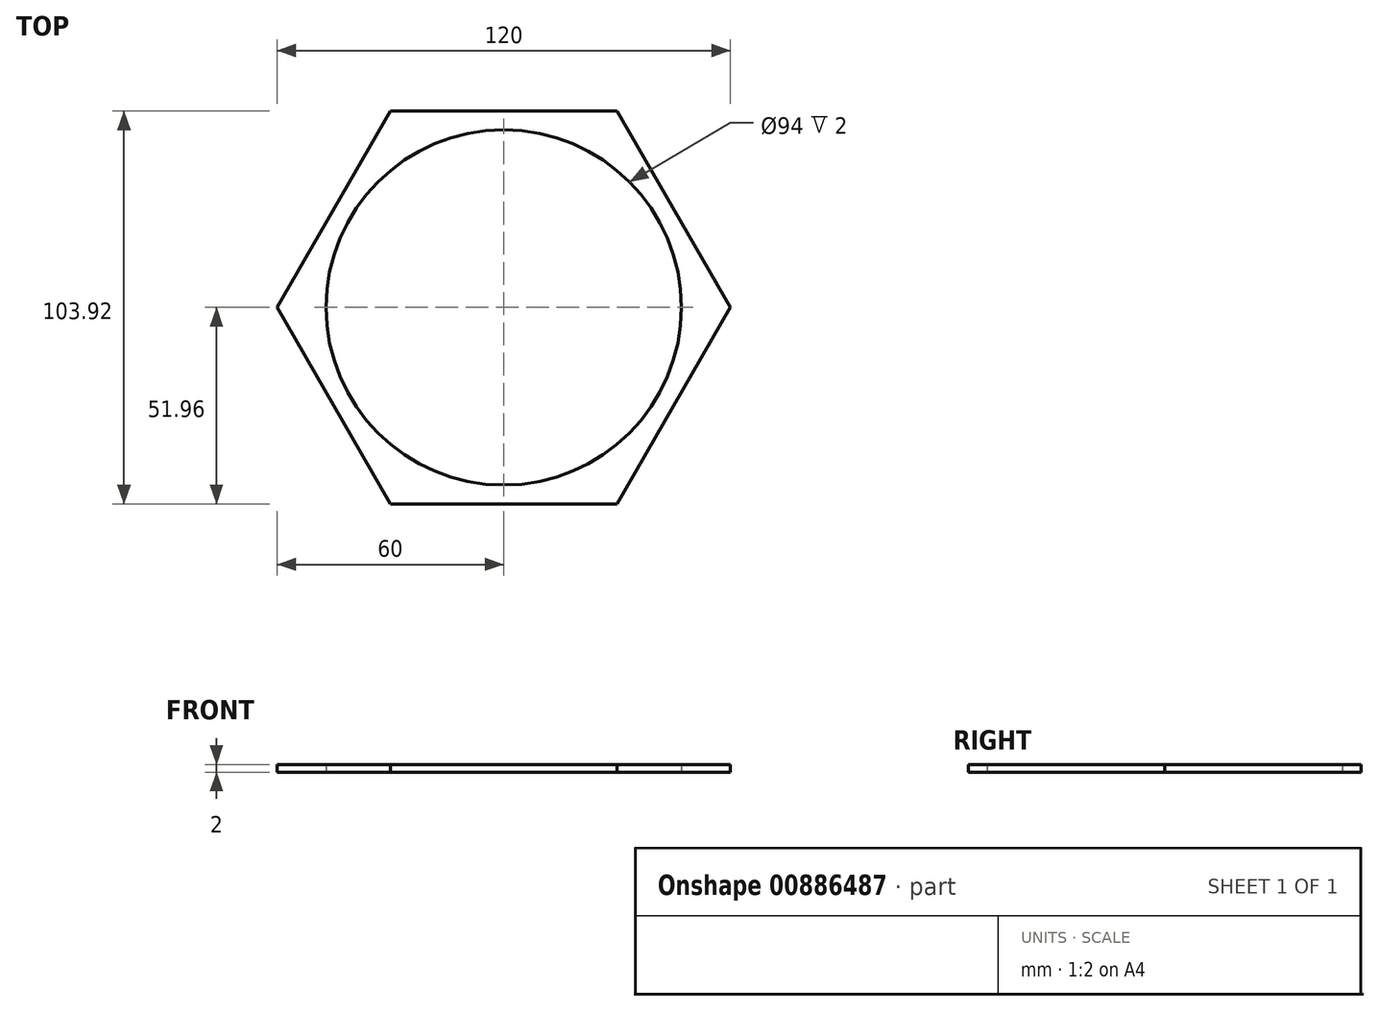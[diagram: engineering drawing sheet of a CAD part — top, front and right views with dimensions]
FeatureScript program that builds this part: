
annotation { "Feature Type Name" : "Feature", "Feature Type Description" : "" }
export const myFeature = defineFeature(function(context is Context, id is Id, definition is map)
    precondition{}
    {
        {
            var Q0;
            Q0=qCreatedBy(makeId("Top.planeOp"),FACE);
            var sketch = newSketch(context, id + "F0", { "sketchPlane" : qUnion([Q0])});
            skCircle(sketch, "E0.cCircle", {"center": v(0, 0) * mm, "radius": 60 * mm, "construction": true});
            skLineSegment(sketch, "E0.0", {"start": v(-60, 0) * mm, "end": v(-30, 51.96) * mm});
            skLineSegment(sketch, "E0.1", {"start": v(-30, 51.96) * mm, "end": v(30, 51.96) * mm});
            skLineSegment(sketch, "E0.2", {"start": v(30, 51.96) * mm, "end": v(60, 0) * mm});
            skLineSegment(sketch, "E0.3", {"start": v(60, 0) * mm, "end": v(30, -51.96) * mm});
            skLineSegment(sketch, "E0.4", {"start": v(30, -51.96) * mm, "end": v(-30, -51.96) * mm});
            skLineSegment(sketch, "E0.5", {"start": v(-30, -51.96) * mm, "end": v(-60, 0) * mm});
            skCircle(sketch, "E1", {"center": v(0, 0) * mm, "radius": 47 * mm});
            skSolve(sketch);
        }
        {
            var Q0;
            Q0=makeQuery(id+"F0.imprint","IMPRINT",FACE,{"disambiguationData":[TD([[makeQuery(id+"F0.imprint","IMPRINT",EDGE,{"derivedFrom":sQuery(id+"F0.wireOp",EDGE,"E0.0")}),-1.0]])]});
            extrude(context, id + "F1", {"entities" : qUnion([Q0]), "depth" : 2 * mm, "offsetDistance" : 25 * mm});
        }
    });
